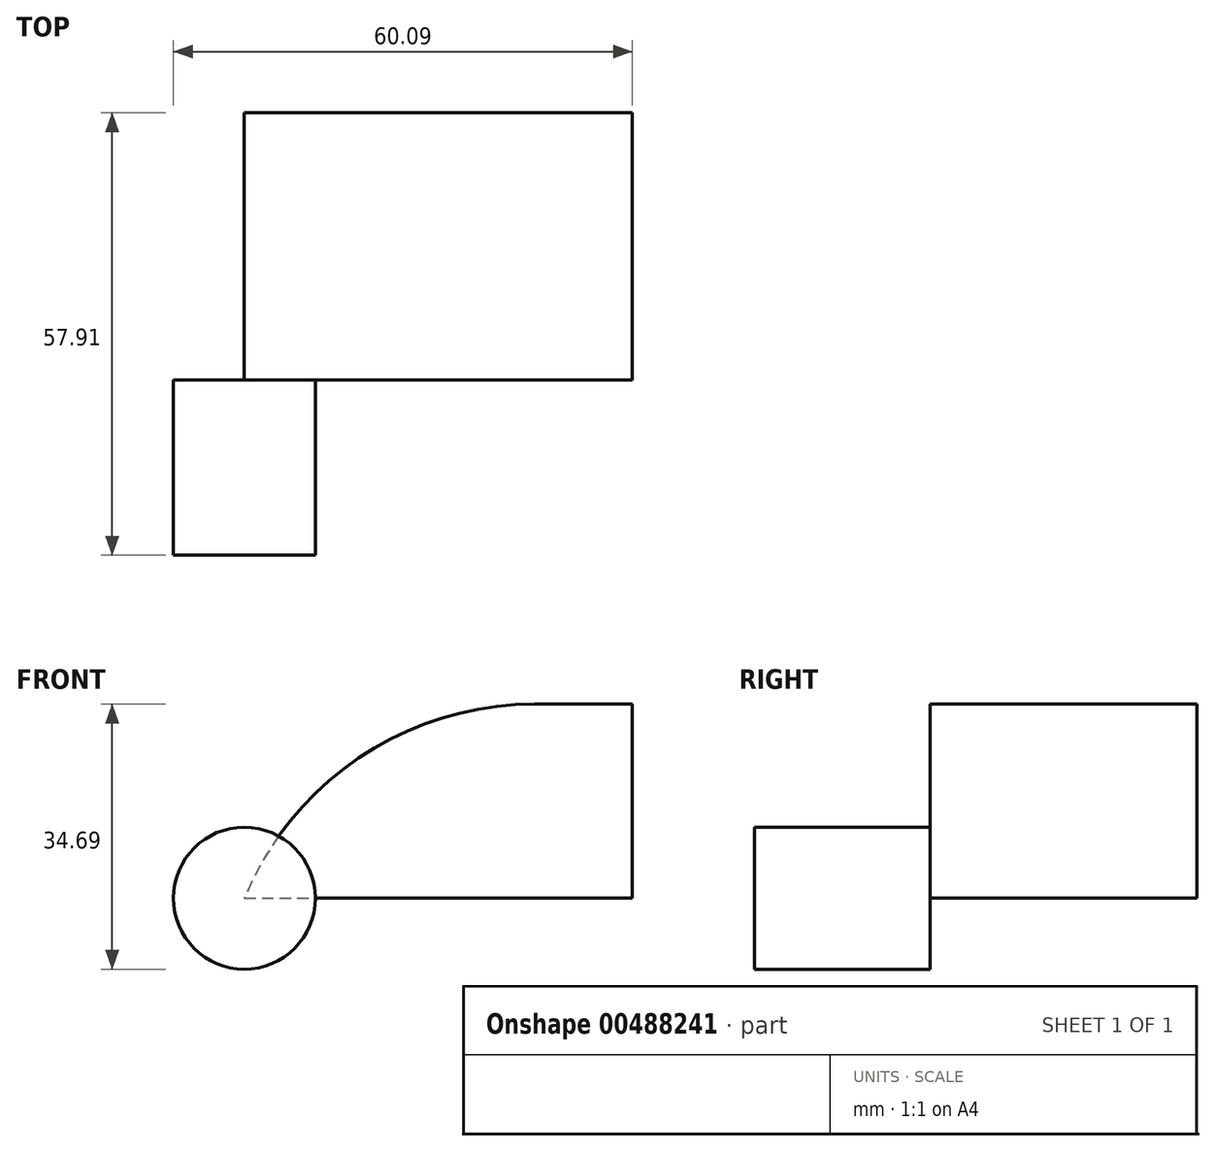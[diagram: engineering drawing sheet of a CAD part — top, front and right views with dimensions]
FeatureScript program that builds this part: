
annotation { "Feature Type Name" : "Feature", "Feature Type Description" : "" }
export const myFeature = defineFeature(function(context is Context, id is Id, definition is map)
    precondition{}
    {
        {
            var Q0;
            Q0=qCreatedBy(makeId("Top.planeOp"),FACE);
            var sketch = newSketch(context, id + "F0", { "sketchPlane" : qUnion([Q0])});
            skLineSegment(sketch, "E0.bottom", {"start": v(0, 0) * mm, "end": v(9.3, 0) * mm});
            skLineSegment(sketch, "E0.top", {"start": v(0, 22.97) * mm, "end": v(9.3, 22.97) * mm});
            skLineSegment(sketch, "E0.left", {"start": v(0, 0) * mm, "end": v(0, 22.97) * mm});
            skLineSegment(sketch, "E0.right", {"start": v(9.3, 0) * mm, "end": v(9.3, 22.97) * mm});
            skLineSegment(sketch, "E1.bottom", {"start": v(9.3, 22.97) * mm, "end": v(60.1, 22.97) * mm});
            skLineSegment(sketch, "E1.top", {"start": v(9.3, 57.9) * mm, "end": v(60.1, 57.9) * mm});
            skLineSegment(sketch, "E1.left", {"start": v(9.3, 22.97) * mm, "end": v(9.3, 57.9) * mm});
            skLineSegment(sketch, "E1.right", {"start": v(60.1, 22.97) * mm, "end": v(60.1, 57.9) * mm});
            skArc(sketch, "E2", {"start": v(9.3, 57.9) * mm, "mid": v(-18.08, 46.48) * mm, "end": v(0, 22.97) * mm});
            skArc(sketch, "E3.0", {"start": v(6.77, 53.5) * mm, "mid": v(-13.17, 45.17) * mm, "end": v(0, 28.05) * mm});
            skSolve(sketch);
        }
        {
            var Q0;
            Q0=makeQuery(id+"F0.imprint","IMPRINT",FACE,{"disambiguationData":[TD([[makeQuery(id+"F0.imprint","IMPRINT",EDGE,{"derivedFrom":sQuery(id+"F0.wireOp",EDGE,"E1.bottom")}),1.0]])]});
            extrude(context, id + "F1", {"entities" : qUnion([Q0]), "depth" : 25.4 * mm});
        }
        {
            var Q0;
            Q0=makeQuery(id+"F0.imprint","IMPRINT",FACE,{"disambiguationData":[TD([[makeQuery(id+"F0.imprint","IMPRINT",EDGE,{"derivedFrom":sQuery(id+"F0.wireOp",EDGE,"E0.bottom")}),1.0]])]});
            var Q1;
            Q1=sQuery(id+"F0.wireOp",EDGE,"E0.right");
            revolve(context, id + "F2", {"operationType" : NewBodyOperationType.ADD, "entities" : qUnion([Q0]), "axis" : qUnion([Q1]), "revolveType" : RevolveType.FULL});
        }
        {
            var Q0;
            Q0=makeQuery(id+"F1.opExtrude","CAP_EDGE",EDGE,{"disambiguationData":[OSD([sQuery(id+"F0.wireOp",EDGE,"E1.left")])],"isStart":false});
            fillet(context, id + "F3", {"entities" : qUnion([Q0]), "radius" : 41.1 * mm, "tangentPropagation" : true, "allowEdgeOverflow" : false});
        }
    });
